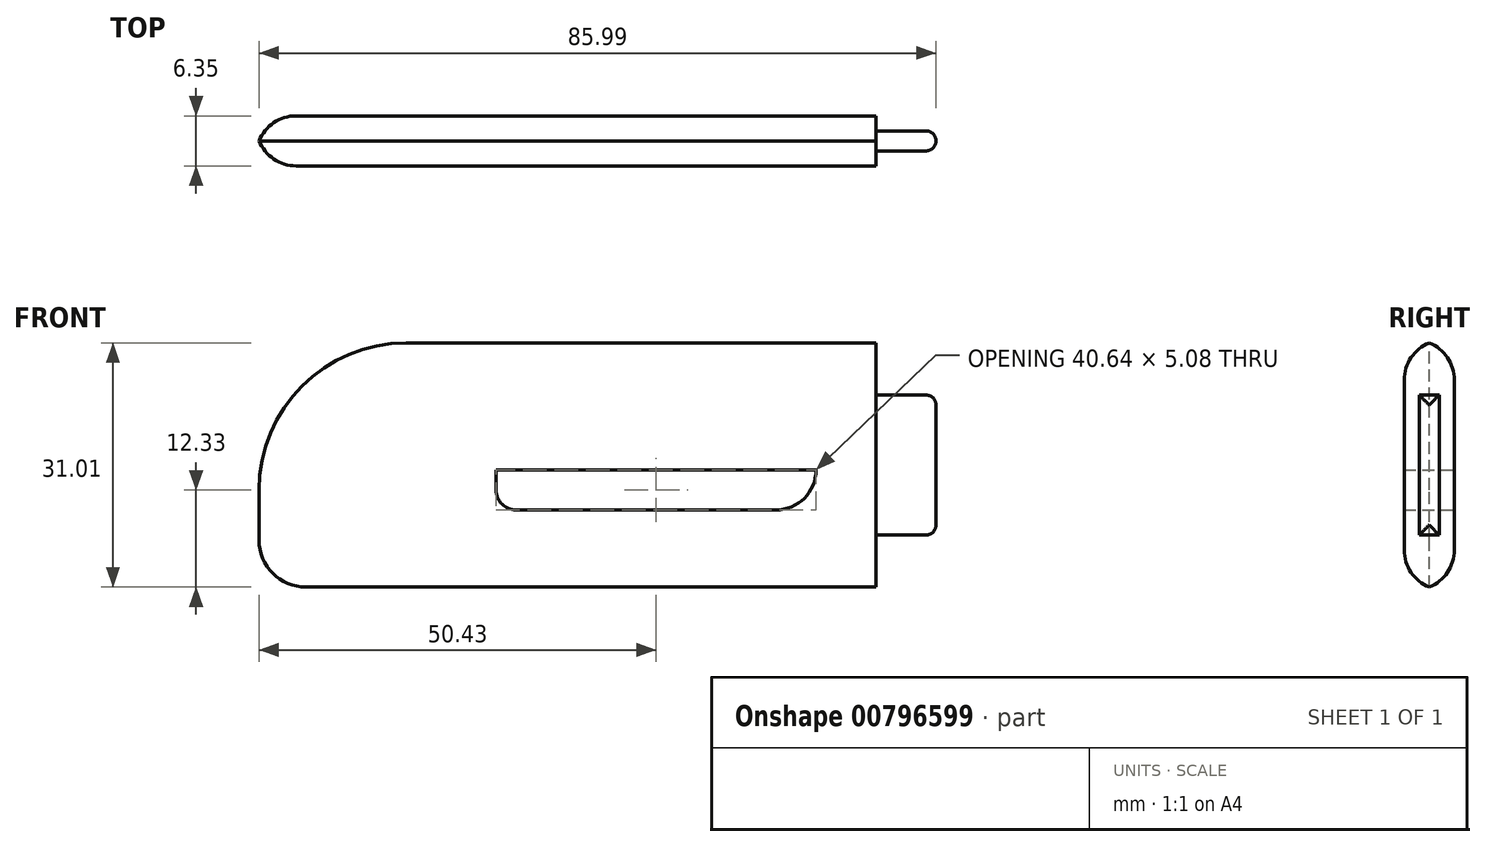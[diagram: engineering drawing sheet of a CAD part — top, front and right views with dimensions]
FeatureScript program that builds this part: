
annotation { "Feature Type Name" : "Feature", "Feature Type Description" : "" }
export const myFeature = defineFeature(function(context is Context, id is Id, definition is map)
    precondition{}
    {
        {
            var Q0;
            Q0=qCreatedBy(makeId("Front.planeOp"),FACE);
            var sketch = newSketch(context, id + "F0", { "sketchPlane" : qUnion([Q0])});
            skLineSegment(sketch, "E0.bottom", {"start": v(20.32, -2.54) * mm, "end": v(-20.32, -2.54) * mm});
            skLineSegment(sketch, "E0.top", {"start": v(20.32, 2.54) * mm, "end": v(-20.32, 2.54) * mm});
            skLineSegment(sketch, "E0.left", {"start": v(20.32, -2.54) * mm, "end": v(20.32, 2.54) * mm});
            skLineSegment(sketch, "E0.right", {"start": v(-20.32, -2.54) * mm, "end": v(-20.32, 2.54) * mm});
            skPoint(sketch, "E0.middle", {"position": v(0, 0) * mm});
            skLineSegment(sketch, "E1", {"start": v(-50.8, 0) * mm, "end": v(-50.8, 0) * mm});
            skLineSegment(sketch, "E2", {"start": v(-50.8, 0) * mm, "end": v(-50.8, -6.35) * mm});
            skLineSegment(sketch, "E3", {"start": v(27.94, 19.05) * mm, "end": v(-31.75, 19.05) * mm});
            skArc(sketch, "E4.filletArc", {"start": v(-31.75, 19.05) * mm, "mid": v(-45.22, 13.47) * mm, "end": v(-50.8, 0) * mm});
            skLineSegment(sketch, "E5", {"start": v(20.32, 19.05) * mm, "end": v(27.94, 19.05) * mm});
            skLineSegment(sketch, "E6", {"start": v(27.94, 19.05) * mm, "end": v(27.94, -12.7) * mm});
            skArc(sketch, "E7.filletArc", {"start": v(-50.8, -6.35) * mm, "mid": v(-48.94, -10.84) * mm, "end": v(-44.45, -12.7) * mm});
            skLineSegment(sketch, "E8", {"start": v(-44.45, -12.7) * mm, "end": v(27.94, -12.7) * mm});
            skSolve(sketch);
        }
        {
            var Q0;
            Q0=makeQuery(id+"F0.imprint","IMPRINT",FACE,{"disambiguationData":[TD([[makeQuery(id+"F0.imprint","IMPRINT",EDGE,{"derivedFrom":sQuery(id+"F0.wireOp",EDGE,"E0.bottom")}),1.0]])]});
            extrude(context, id + "F1", {"entities" : qUnion([Q0]), "depth" : 6.35 * mm, "offsetDistance" : 25.4 * mm});
        }
        {
            var Q0;
            Q0=makeQuery(id+"F1.opExtrude","SWEPT_FACE",FACE,{"disambiguationData":[OSD([sQuery(id+"F0.wireOp",EDGE,"E6")])]});
            var sketch = newSketch(context, id + "F2", { "sketchPlane" : qUnion([Q0])});
            skLineSegment(sketch, "E9.0", {"start": v(-6.35, 19.05) * mm, "end": v(-6.35, -12.7) * mm});
            skLineSegment(sketch, "E10.0", {"start": v(0, 19.05) * mm, "end": v(0, -12.7) * mm});
            skLineSegment(sketch, "E11.0.0", {"start": v(0, -12.7) * mm, "end": v(0, 19.05) * mm});
            skLineSegment(sketch, "E11.0.1", {"start": v(0, 19.05) * mm, "end": v(-6.35, 19.05) * mm});
            skLineSegment(sketch, "E11.0.3", {"start": v(-6.35, -12.7) * mm, "end": v(0, -12.7) * mm});
            skLineSegment(sketch, "E12", {"start": v(-3.18, 3.17) * mm, "end": v(-3.18, -12.7) * mm});
            skPoint(sketch, "E12.startSnap0", {"position": v(-3.18, 19.05) * mm});
            skPoint(sketch, "E12.startSnap1", {"position": v(0, 3.17) * mm});
            skLineSegment(sketch, "E13.bottom", {"start": v(-4.45, 12.06) * mm, "end": v(-1.9, 12.06) * mm});
            skLineSegment(sketch, "E13.top", {"start": v(-4.44, -5.72) * mm, "end": v(-1.9, -5.72) * mm});
            skLineSegment(sketch, "E13.left", {"start": v(-4.45, 12.06) * mm, "end": v(-4.44, -5.72) * mm});
            skLineSegment(sketch, "E13.right", {"start": v(-1.9, 12.06) * mm, "end": v(-1.9, -5.72) * mm});
            skPoint(sketch, "E13.middle", {"position": v(-3.18, 3.17) * mm});
            skSolve(sketch);
        }
        {
            var Q0;
            Q0=makeQuery(id+"F2.imprint","IMPRINT",FACE,{"disambiguationData":[TD([[makeQuery(id+"F2.imprint","IMPRINT",EDGE,{"derivedFrom":sQuery(id+"F2.wireOp",EDGE,"E13.bottom")}),-1.0]])]});
            extrude(context, id + "F3", {"entities" : qUnion([Q0]), "operationType" : NewBodyOperationType.ADD, "depth" : 7.62 * mm, "offsetDistance" : 25.4 * mm});
        }
        {
            var Q0;
            Q0=makeQuery(id+"F3.opExtrude","CAP_EDGE",EDGE,{"disambiguationData":[OSD([sQuery(id+"F2.wireOp",EDGE,"E13.left")])],"isStart":false});
            var Q1;
            Q1=makeQuery(id+"F3.opExtrude","CAP_EDGE",EDGE,{"disambiguationData":[OSD([sQuery(id+"F2.wireOp",EDGE,"E13.bottom")])],"isStart":false});
            var Q2;
            Q2=makeQuery(id+"F3.opExtrude","CAP_EDGE",EDGE,{"disambiguationData":[OSD([sQuery(id+"F2.wireOp",EDGE,"E13.right")])],"isStart":false});
            var Q3;
            Q3=makeQuery(id+"F3.opExtrude","CAP_EDGE",EDGE,{"disambiguationData":[OSD([sQuery(id+"F2.wireOp",EDGE,"E13.top")])],"isStart":false});
            fillet(context, id + "F4", {"entities" : qUnion([Q0, Q1, Q2, Q3]), "radius" : 1.27 * mm, "tangentPropagation" : true, "allowEdgeOverflow" : false});
        }
        {
            var Q0;
            Q0=makeQuery(id+"F1.opExtrude","CAP_EDGE",EDGE,{"disambiguationData":[OSD([sQuery(id+"F0.wireOp",EDGE,"E7.filletArc")])],"isStart":false});
            var Q1;
            Q1=makeQuery(id+"F1.opExtrude","CAP_EDGE",EDGE,{"disambiguationData":[OSD([sQuery(id+"F0.wireOp",EDGE,"E2")])],"isStart":true});
            fillet(context, id + "F5", {"entities" : qUnion([Q0, Q1]), "radius" : 5.08 * mm, "tangentPropagation" : true, "allowEdgeOverflow" : false});
        }
        {
            var Q0;
            Q0=makeQuery(id+"F1.opExtrude","SWEPT_EDGE",EDGE,{"disambiguationData":[OSD([sQuery(id+"F0.wireOp",EDGE,"E0.bottom"),sQuery(id+"F0.wireOp",EDGE,"E0.left")])]});
            fillet(context, id + "F6", {"entities" : qUnion([Q0]), "radius" : 5.08 * mm, "tangentPropagation" : true, "allowEdgeOverflow" : false});
        }
        {
            var Q0;
            Q0=makeQuery(id+"F1.opExtrude","SWEPT_EDGE",EDGE,{"disambiguationData":[OSD([sQuery(id+"F0.wireOp",EDGE,"E0.bottom"),sQuery(id+"F0.wireOp",EDGE,"E0.right")])]});
            fillet(context, id + "F7", {"entities" : qUnion([Q0]), "radius" : 2.54 * mm, "tangentPropagation" : true, "allowEdgeOverflow" : false});
        }
    });
